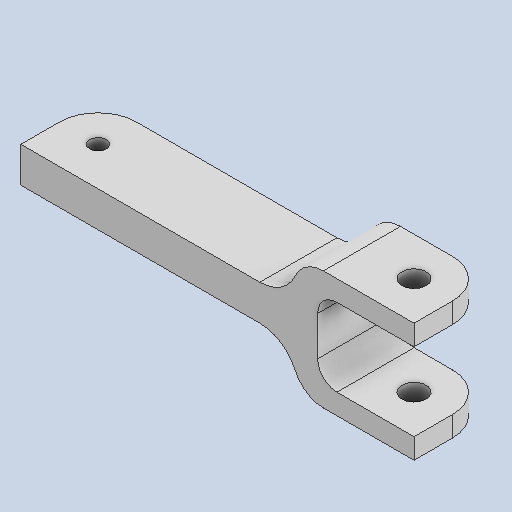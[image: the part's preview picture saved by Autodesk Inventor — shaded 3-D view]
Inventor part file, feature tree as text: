
AUTODESK INVENTOR PART (.ipt)
format: ipt  version: 2022 (Build 260153000, 153)  size: 118,784 bytes
history: native  units: in
note: dims shown in document units (in); Inventor stores cm internally (conversion verified against a paired STEP export)
features: fillet x1
ambient origin geometry x8: Origin, YZ Plane, XZ Plane, XY Plane, X Axis, Y Axis, Z Axis, Center Point
bodies: Solid1 (feature_tree)
feature tree (1):
  fillet  "Fillet8"  [1 undecoded]
note: 1 required parameter value undecoded (feature->parameter linkage not recoverable at this tier; creation-order binding heuristic only, values carry confidence <= 0.55)
